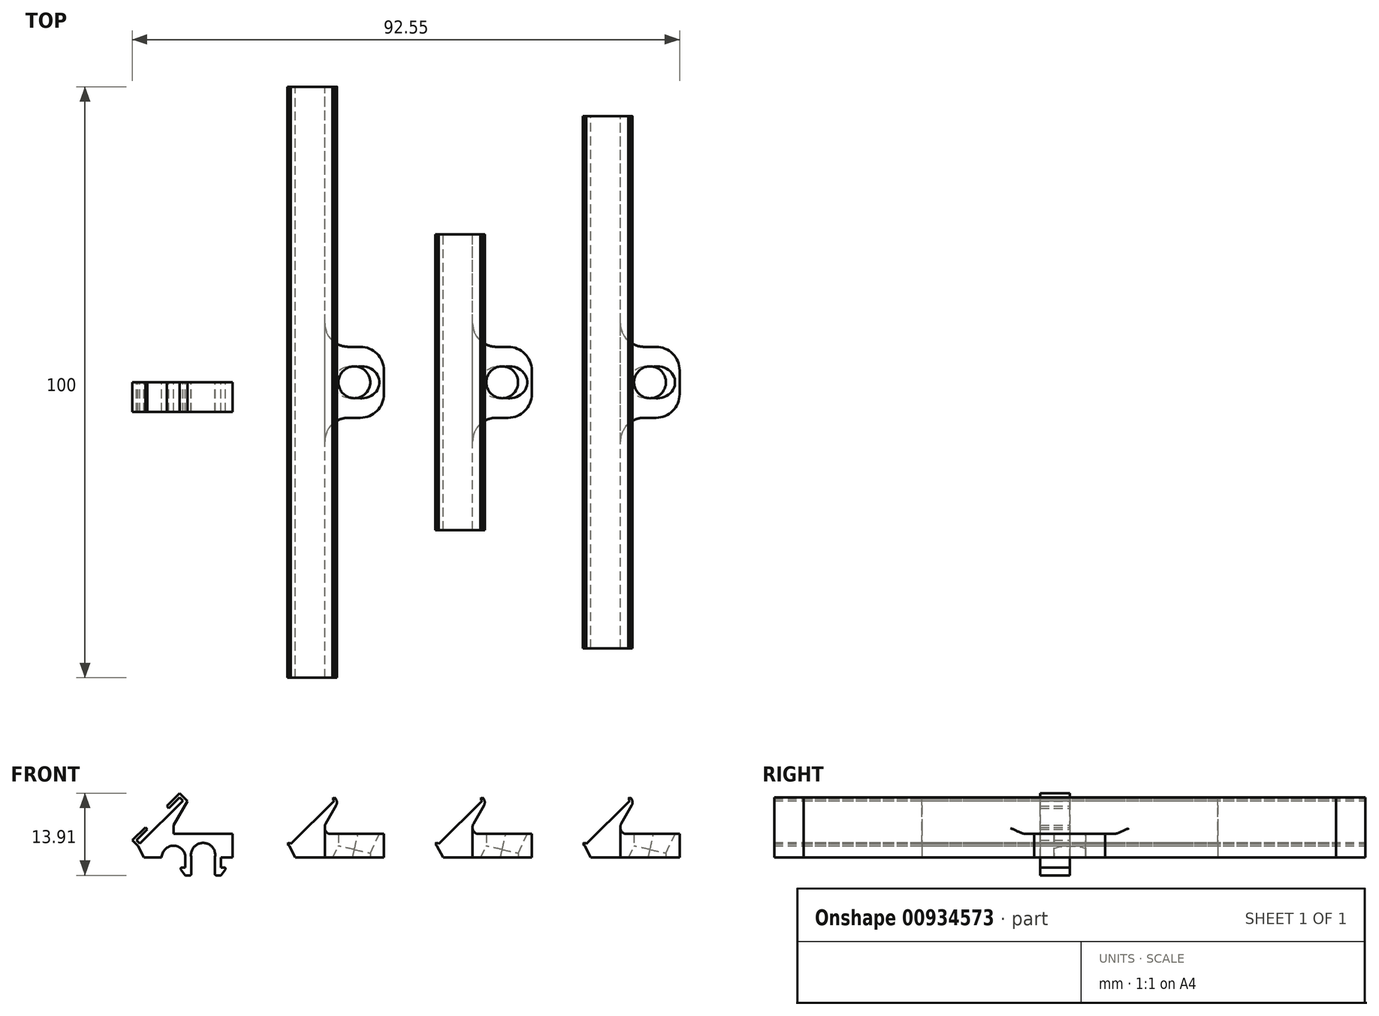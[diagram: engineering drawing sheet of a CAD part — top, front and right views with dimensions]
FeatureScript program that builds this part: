
annotation { "Feature Type Name" : "Feature", "Feature Type Description" : "" }
export const myFeature = defineFeature(function(context is Context, id is Id, definition is map)
    precondition{}
    {
        {
            var Q0;
            Q0=qCreatedBy(makeId("Front.planeOp"),FACE);
            var sketch = newSketch(context, id + "F0", { "sketchPlane" : qUnion([Q0])});
            skLineSegment(sketch, "E0", {"start": v(0, 0) * mm, "end": v(-10, 0) * mm});
            skLineSegment(sketch, "E1", {"start": v(-11.04, 2.57) * mm, "end": v(-10.76, 2.28) * mm});
            skLineSegment(sketch, "E2", {"start": v(-10.76, 2.28) * mm, "end": v(-3.4, 9.64) * mm});
            skLineSegment(sketch, "E3", {"start": v(-3.4, 9.64) * mm, "end": v(-3.69, 9.92) * mm});
            skLineSegment(sketch, "E4", {"start": v(-11.04, 2.57) * mm, "end": v(-11.33, 2.28) * mm});
            skLineSegment(sketch, "E5", {"start": v(-2.7, 4) * mm, "end": v(5, 4) * mm});
            skLineSegment(sketch, "E6", {"start": v(5, 4) * mm, "end": v(5, 0) * mm});
            skLineSegment(sketch, "E7", {"start": v(5, 0) * mm, "end": v(0, 0) * mm});
            skLineSegment(sketch, "E8", {"start": v(-2.7, 9.5) * mm, "end": v(-5, 5.5) * mm});
            skLineSegment(sketch, "E9", {"start": v(-5, 5.5) * mm, "end": v(-5, 4) * mm});
            skLineSegment(sketch, "E10", {"start": v(-5, 4) * mm, "end": v(-2.7, 4) * mm});
            skLineSegment(sketch, "E11", {"start": v(-3.69, 9.92) * mm, "end": v(-3.4, 10.2) * mm});
            skLineSegment(sketch, "E12", {"start": v(-3.4, 10.2) * mm, "end": v(-2.7, 9.5) * mm});
            skLineSegment(sketch, "E13", {"start": v(-2.7, 4) * mm, "end": v(-2.7, 0) * mm});
            skLineSegment(sketch, "E14", {"start": v(-5, 4) * mm, "end": v(-5, 0) * mm});
            skLineSegment(sketch, "E15", {"start": v(-11.33, 2.28) * mm, "end": v(-11.04, 2) * mm});
            skLineSegment(sketch, "E16", {"start": v(-11.04, 2) * mm, "end": v(-10, 0) * mm});
            skLineSegment(sketch, "E17", {"start": v(0, 0) * mm, "end": v(6.82, 14.44) * mm, "construction": true});
            skSolve(sketch);
        }
        {
            var Q0;
            Q0=makeQuery(id+"F0.imprint","IMPRINT",FACE,{"disambiguationData":[TD([[makeQuery(id+"F0.imprint","IMPRINT",EDGE,{"derivedFrom":sQuery(id+"F0.wireOp",EDGE,"E1")}),-1.0]])]});
            var Q1;
            Q1=makeQuery(id+"F0.imprint","IMPRINT",FACE,{"disambiguationData":[TD([[makeQuery(id+"F0.imprint","IMPRINT",EDGE,{"derivedFrom":sQuery(id+"F0.wireOp",EDGE,"E5")}),-1.0]])]});
            var Q2;
            Q2=makeQuery(id+"F0.imprint","IMPRINT",FACE,{"disambiguationData":[TD([[makeQuery(id+"F0.imprint","IMPRINT",EDGE,{"derivedFrom":sQuery(id+"F0.wireOp",EDGE,"E10")}),-1.0]])]});
            extrude(context, id + "F1", {"entities" : qUnion([Q0, Q1, Q2]), "endBound" : BoundingType.SYMMETRIC, "depth" : 12 * mm, "offsetDistance" : 25 * mm});
        }
        {
            var Q0;
            Q0=qCreatedBy(makeId("Top.planeOp"),FACE);
            var sketch = newSketch(context, id + "F2", { "sketchPlane" : qUnion([Q0])});
            skCircle(sketch, "E18", {"center": v(0, 0) * mm, "radius": 2.7 * mm});
            skSolve(sketch);
        }
        {
            var Q0;
            Q0=makeQuery(id+"F2.imprint","IMPRINT",FACE,{"disambiguationData":[TD([[makeQuery(id+"F2.imprint","IMPRINT",EDGE,{"derivedFrom":sQuery(id+"F2.wireOp",EDGE,"E18")}),1.0]])]});
            extrude(context, id + "F3", {"entities" : qUnion([Q0]), "operationType" : NewBodyOperationType.REMOVE, "depth" : 25 * mm, "offsetDistance" : 25 * mm});
        }
        {
            var Q0;
            Q0=makeQuery(id+"F0.imprint","IMPRINT",FACE,{"disambiguationData":[TD([[makeQuery(id+"F0.imprint","IMPRINT",EDGE,{"derivedFrom":sQuery(id+"F0.wireOp",EDGE,"E1")}),-1.0]])]});
            extrude(context, id + "F4", {"entities" : qUnion([Q0]), "operationType" : NewBodyOperationType.ADD, "endBound" : BoundingType.SYMMETRIC, "depth" : 100 * mm, "offsetDistance" : 25 * mm});
        }
        {
            var Q0;
            {var subQ0=sQuery(id+"F0.wireOp",EDGE,"E9");Q0=makeQuery(id+"F4.boolean.opBoolean","INTERSECT",EDGE,{"derivedFrom":[makeQuery(id+"F1.opExtrude","CAP_FACE",FACE,{"disambiguationData":[OSD([sQuery(id+"F0.wireOp",EDGE,"E0"),sQuery(id+"F0.wireOp",EDGE,"E1"),sQuery(id+"F0.wireOp",EDGE,"E2"),sQuery(id+"F0.wireOp",EDGE,"E3"),sQuery(id+"F0.wireOp",EDGE,"E4"),sQuery(id+"F0.wireOp",EDGE,"E5"),sQuery(id+"F0.wireOp",EDGE,"E6"),sQuery(id+"F0.wireOp",EDGE,"E7"),sQuery(id+"F0.wireOp",EDGE,"E8"),subQ0,sQuery(id+"F0.wireOp",EDGE,"E10"),sQuery(id+"F0.wireOp",EDGE,"E11"),sQuery(id+"F0.wireOp",EDGE,"E12"),sQuery(id+"F0.wireOp",EDGE,"E15"),sQuery(id+"F0.wireOp",EDGE,"E16")])],"isStart":true}),makeQuery(id+"F4.opExtrude","SWEPT_FACE",FACE,{"disambiguationData":[OSD([subQ0,sQuery(id+"F0.wireOp",EDGE,"E14")])]})]});}
            var Q1;
            Q1=makeQuery(id+"F1.opExtrude","CAP_EDGE",EDGE,{"disambiguationData":[OSD([sQuery(id+"F0.wireOp",EDGE,"E6")])],"isStart":true});
            var Q2;
            Q2=makeQuery(id+"F1.opExtrude","CAP_EDGE",EDGE,{"disambiguationData":[OSD([sQuery(id+"F0.wireOp",EDGE,"E6")])],"isStart":false});
            var Q3;
            {var subQ0=sQuery(id+"F0.wireOp",EDGE,"E9");Q3=makeQuery(id+"F4.boolean.opBoolean","INTERSECT",EDGE,{"derivedFrom":[makeQuery(id+"F1.opExtrude","CAP_FACE",FACE,{"disambiguationData":[OSD([sQuery(id+"F0.wireOp",EDGE,"E0"),sQuery(id+"F0.wireOp",EDGE,"E1"),sQuery(id+"F0.wireOp",EDGE,"E2"),sQuery(id+"F0.wireOp",EDGE,"E3"),sQuery(id+"F0.wireOp",EDGE,"E4"),sQuery(id+"F0.wireOp",EDGE,"E5"),sQuery(id+"F0.wireOp",EDGE,"E6"),sQuery(id+"F0.wireOp",EDGE,"E7"),sQuery(id+"F0.wireOp",EDGE,"E8"),subQ0,sQuery(id+"F0.wireOp",EDGE,"E10"),sQuery(id+"F0.wireOp",EDGE,"E11"),sQuery(id+"F0.wireOp",EDGE,"E12"),sQuery(id+"F0.wireOp",EDGE,"E15"),sQuery(id+"F0.wireOp",EDGE,"E16")])],"isStart":false}),makeQuery(id+"F4.opExtrude","SWEPT_FACE",FACE,{"disambiguationData":[OSD([subQ0,sQuery(id+"F0.wireOp",EDGE,"E14")])]})]});}
            fillet(context, id + "F5", {"entities" : qUnion([Q0, Q1, Q2, Q3]), "radius" : 4 * mm, "tangentPropagation" : true, "allowEdgeOverflow" : false});
        }
        {
            var Q0;
            {var subQ0=sQuery(id+"F0.wireOp",EDGE,"E12");var subQ1=sQuery(id+"F0.wireOp",EDGE,"E8");var subQ2=sQuery(id+"F0.wireOp",EDGE,"E16");var subQ3=sQuery(id+"F0.wireOp",EDGE,"E15");var subQ4=sQuery(id+"F0.wireOp",EDGE,"E11");var subQ5=sQuery(id+"F0.wireOp",EDGE,"E10");var subQ6=sQuery(id+"F0.wireOp",EDGE,"E9");var subQ7=sQuery(id+"F0.wireOp",EDGE,"E7");var subQ8=sQuery(id+"F0.wireOp",EDGE,"E6");var subQ9=sQuery(id+"F0.wireOp",EDGE,"E5");var subQ10=sQuery(id+"F0.wireOp",EDGE,"E4");var subQ11=sQuery(id+"F0.wireOp",EDGE,"E3");var subQ12=sQuery(id+"F0.wireOp",EDGE,"E2");var subQ13=sQuery(id+"F0.wireOp",EDGE,"E1");var subQ14=sQuery(id+"F0.wireOp",EDGE,"E0");var subQ17=makeQuery(id+"F1.opExtrude","SWEPT_EDGE",EDGE,{"disambiguationData":[OSD([subQ1,subQ0])]});Q0=makeQuery(id+"F4.boolean.opBoolean","MERGE",EDGE,{"derivedFrom":[makeQuery(id+"F3.boolean.opBoolean","SPLIT",EDGE,{"disambiguationData":[TD([makeQuery(id+"F1.opExtrude","CAP_FACE",FACE,{"disambiguationData":[OSD([subQ14,subQ13,subQ12,subQ11,subQ10,subQ9,subQ8,subQ7,subQ1,subQ6,subQ5,subQ4,subQ0,subQ3,subQ2])],"isStart":true})])],"derivedFrom":subQ17}),makeQuery(id+"F3.boolean.opBoolean","SPLIT",EDGE,{"disambiguationData":[TD([makeQuery(id+"F1.opExtrude","CAP_FACE",FACE,{"disambiguationData":[OSD([subQ14,subQ13,subQ12,subQ11,subQ10,subQ9,subQ8,subQ7,subQ1,subQ6,subQ5,subQ4,subQ0,subQ3,subQ2])],"isStart":false})])],"derivedFrom":subQ17}),makeQuery(id+"F4.opExtrude","SWEPT_EDGE",EDGE,{"disambiguationData":[OSD([subQ1,subQ0])]})]});}
            var Q1;
            {var subQ0=sQuery(id+"F0.wireOp",EDGE,"E9");var subQ1=sQuery(id+"F0.wireOp",EDGE,"E8");Q1=makeQuery(id+"F4.boolean.opBoolean","MERGE",EDGE,{"derivedFrom":[makeQuery(id+"F1.opExtrude","SWEPT_EDGE",EDGE,{"disambiguationData":[OSD([subQ1,subQ0])]}),makeQuery(id+"F4.opExtrude","SWEPT_EDGE",EDGE,{"disambiguationData":[OSD([subQ1,subQ0])]})]});}
            var Q2;
            Q2=makeQuery(id+"F1.opExtrude","SWEPT_EDGE",EDGE,{"disambiguationData":[OSD([sQuery(id+"F0.wireOp",EDGE,"E9"),sQuery(id+"F0.wireOp",EDGE,"E10"),sQuery(id+"F0.wireOp",EDGE,"E14")])]});
            fillet(context, id + "F6", {"entities" : qUnion([Q0, Q1, Q2]), "radius" : 1 * mm, "tangentPropagation" : true, "allowEdgeOverflow" : false});
        }
        {
            var Q0;
            Q0=sQuery(id+"F0.wireOp",EDGE,"E17");
            cPlane(context, id + "F7", {"entities" : qUnion([Q0]), "cplaneType" : CPlaneType.MID_PLANE, "offset" : 25 * mm, "width" : 150 * mm, "height" : 150 * mm});
        }
        {
            var Q0;
            Q0=qCreatedBy(id+"F7.planeOp",FACE);
            var sketch = newSketch(context, id + "F8", { "sketchPlane" : qUnion([Q0])});
            skCircle(sketch, "E19", {"center": v(-0.58, 0) * mm, "radius": 2.7 * mm});
            skSolve(sketch);
        }
        {
            var Q0;
            Q0=makeQuery(id+"F8.imprint","IMPRINT",FACE,{"disambiguationData":[TD([[makeQuery(id+"F8.imprint","IMPRINT",EDGE,{"derivedFrom":sQuery(id+"F8.wireOp",EDGE,"E19")}),1.0]])]});
            extrude(context, id + "F9", {"entities" : qUnion([Q0]), "operationType" : NewBodyOperationType.REMOVE, "oppositeDirection" : true, "depth" : 25 * mm, "offsetDistance" : 25 * mm});
        }
        {
            var Q0;
            Q0=makeQuery(id+"F1.opExtrude","SWEPT_BODY",BODY,{"disambiguationData":[OSD([sQuery(id+"F0.wireOp",EDGE,"E0"),sQuery(id+"F0.wireOp",EDGE,"E1"),sQuery(id+"F0.wireOp",EDGE,"E2"),sQuery(id+"F0.wireOp",EDGE,"E3"),sQuery(id+"F0.wireOp",EDGE,"E4"),sQuery(id+"F0.wireOp",EDGE,"E5"),sQuery(id+"F0.wireOp",EDGE,"E6"),sQuery(id+"F0.wireOp",EDGE,"E7"),sQuery(id+"F0.wireOp",EDGE,"E8"),sQuery(id+"F0.wireOp",EDGE,"E9"),sQuery(id+"F0.wireOp",EDGE,"E10"),sQuery(id+"F0.wireOp",EDGE,"E11"),sQuery(id+"F0.wireOp",EDGE,"E12"),sQuery(id+"F0.wireOp",EDGE,"E15"),sQuery(id+"F0.wireOp",EDGE,"E16")])]});
            transform(context, id + "F10", {"entities" : qUnion([Q0]), "transformType" : TransformType.TRANSLATION_3D, "dx" : 25 * mm, "dy" : 0 * mm, "dz" : 0 * mm, "makeCopy" : true});
        }
        {
            var Q0;
            Q0=makeQuery(id+"F10.opPattern","COPY",FACE,{"derivedFrom":makeQuery(id+"F4.opExtrude","CAP_FACE",FACE,{"disambiguationData":[OSD([sQuery(id+"F0.wireOp",EDGE,"E0"),sQuery(id+"F0.wireOp",EDGE,"E1"),sQuery(id+"F0.wireOp",EDGE,"E2"),sQuery(id+"F0.wireOp",EDGE,"E3"),sQuery(id+"F0.wireOp",EDGE,"E4"),sQuery(id+"F0.wireOp",EDGE,"E8"),sQuery(id+"F0.wireOp",EDGE,"E9"),sQuery(id+"F0.wireOp",EDGE,"E11"),sQuery(id+"F0.wireOp",EDGE,"E12"),sQuery(id+"F0.wireOp",EDGE,"E14"),sQuery(id+"F0.wireOp",EDGE,"E15"),sQuery(id+"F0.wireOp",EDGE,"E16")])],"isStart":false}),"instanceName":"1"});
            var Q1;
            Q1=makeQuery(id+"F10.opPattern","COPY",FACE,{"derivedFrom":makeQuery(id+"F4.opExtrude","CAP_FACE",FACE,{"disambiguationData":[OSD([sQuery(id+"F0.wireOp",EDGE,"E0"),sQuery(id+"F0.wireOp",EDGE,"E1"),sQuery(id+"F0.wireOp",EDGE,"E2"),sQuery(id+"F0.wireOp",EDGE,"E3"),sQuery(id+"F0.wireOp",EDGE,"E4"),sQuery(id+"F0.wireOp",EDGE,"E8"),sQuery(id+"F0.wireOp",EDGE,"E9"),sQuery(id+"F0.wireOp",EDGE,"E11"),sQuery(id+"F0.wireOp",EDGE,"E12"),sQuery(id+"F0.wireOp",EDGE,"E14"),sQuery(id+"F0.wireOp",EDGE,"E15"),sQuery(id+"F0.wireOp",EDGE,"E16")])],"isStart":true}),"instanceName":"1"});
            extrude(context, id + "F11", {"entities" : qUnion([Q0, Q1]), "operationType" : NewBodyOperationType.REMOVE, "endBound" : BoundingType.SYMMETRIC, "oppositeDirection" : true, "depth" : 50 * mm, "offsetDistance" : 25 * mm});
        }
        {
            var Q0;
            Q0=qCreatedBy(makeId("Front.planeOp"),FACE);
            var sketch = newSketch(context, id + "F12", { "sketchPlane" : qUnion([Q0])});
            skLineSegment(sketch, "E20", {"start": v(-25.58, 0) * mm, "end": v(-35.58, 0) * mm});
            skLineSegment(sketch, "E21", {"start": v(-36.84, 2.92) * mm, "end": v(-36.27, 2.35) * mm});
            skLineSegment(sketch, "E22", {"start": v(-36.27, 2.35) * mm, "end": v(-28.99, 9.64) * mm});
            skLineSegment(sketch, "E23", {"start": v(-28.99, 9.64) * mm, "end": v(-29.56, 10.2) * mm});
            skLineSegment(sketch, "E24", {"start": v(-36.84, 2.92) * mm, "end": v(-37.2, 2.57) * mm});
            skLineSegment(sketch, "E25", {"start": v(-28.28, 4) * mm, "end": v(-20.58, 4) * mm});
            skLineSegment(sketch, "E26", {"start": v(-20.58, 4) * mm, "end": v(-20.58, 0) * mm});
            skLineSegment(sketch, "E27", {"start": v(-20.58, 0) * mm, "end": v(-25.58, 0) * mm});
            skLineSegment(sketch, "E28", {"start": v(-28.21, 9.57) * mm, "end": v(-30.58, 5.5) * mm});
            skLineSegment(sketch, "E29", {"start": v(-30.58, 5.5) * mm, "end": v(-30.58, 4) * mm});
            skLineSegment(sketch, "E30", {"start": v(-30.58, 4) * mm, "end": v(-28.28, 4) * mm});
            skLineSegment(sketch, "E31", {"start": v(-29.56, 10.2) * mm, "end": v(-29.2, 10.56) * mm});
            skLineSegment(sketch, "E32", {"start": v(-29.2, 10.56) * mm, "end": v(-28.21, 9.57) * mm});
            skLineSegment(sketch, "E33", {"start": v(-28.28, 4) * mm, "end": v(-28.28, 0) * mm});
            skLineSegment(sketch, "E34", {"start": v(-30.58, 4) * mm, "end": v(-30.58, 0) * mm});
            skLineSegment(sketch, "E35", {"start": v(-37.2, 2.57) * mm, "end": v(-36.63, 2) * mm});
            skLineSegment(sketch, "E36", {"start": v(-36.63, 2) * mm, "end": v(-35.58, 0) * mm});
            skLineSegment(sketch, "E37", {"start": v(-25.58, 0) * mm, "end": v(-25.58, 24.72) * mm, "construction": true});
            skLineSegment(sketch, "E38", {"start": v(-25.58, 15.93) * mm, "end": v(-25.58, -11.5) * mm, "construction": true});
            skLineSegment(sketch, "E39", {"start": v(-27.58, 0) * mm, "end": v(-27.58, -3) * mm});
            skLineSegment(sketch, "E40", {"start": v(-27.58, -3) * mm, "end": v(-28.58, -3) * mm});
            skLineSegment(sketch, "E41", {"start": v(-28.58, -3) * mm, "end": v(-29.58, -1.7) * mm});
            skLineSegment(sketch, "E42", {"start": v(-29.58, -1.7) * mm, "end": v(-28.58, -1.7) * mm});
            skLineSegment(sketch, "E43", {"start": v(-28.58, -1.7) * mm, "end": v(-28.58, 0) * mm});
            skArc(sketch, "E44", {"start": v(-27.58, 0) * mm, "mid": v(-25.58, 2.49) * mm, "end": v(-23.58, 0) * mm});
            skArc(sketch, "E45", {"start": v(-28.58, 0) * mm, "mid": v(-30.58, 2) * mm, "end": v(-32.58, 0) * mm});
            skLineSegment(sketch, "E46", {"start": v(-36.84, 2.92) * mm, "end": v(-35, 4.76) * mm});
            skLineSegment(sketch, "E47", {"start": v(-35, 4.76) * mm, "end": v(-35.35, 5.11) * mm});
            skLineSegment(sketch, "E48", {"start": v(-35.35, 5.11) * mm, "end": v(-37.55, 2.92) * mm});
            skLineSegment(sketch, "E49", {"start": v(-37.55, 2.92) * mm, "end": v(-37.2, 2.57) * mm});
            skLineSegment(sketch, "E50", {"start": v(-29.56, 10.2) * mm, "end": v(-31.4, 8.36) * mm});
            skLineSegment(sketch, "E51", {"start": v(-31.4, 8.36) * mm, "end": v(-31.75, 8.72) * mm});
            skLineSegment(sketch, "E52", {"start": v(-31.75, 8.72) * mm, "end": v(-29.56, 10.9) * mm});
            skLineSegment(sketch, "E53", {"start": v(-29.56, 10.9) * mm, "end": v(-29.2, 10.56) * mm});
            skLineSegment(sketch, "E54.MirrorCS", {"start": v(-23.58, 0) * mm, "end": v(-23.58, -3) * mm});
            skLineSegment(sketch, "E55.MirrorCS", {"start": v(-23.58, -3) * mm, "end": v(-22.58, -3) * mm});
            skLineSegment(sketch, "E56.MirrorCS", {"start": v(-22.58, -3) * mm, "end": v(-21.58, -1.7) * mm});
            skLineSegment(sketch, "E57.MirrorCS", {"start": v(-21.58, -1.7) * mm, "end": v(-22.58, -1.7) * mm});
            skLineSegment(sketch, "E58.MirrorCS", {"start": v(-22.58, -1.7) * mm, "end": v(-22.58, 0) * mm});
            skSolve(sketch);
        }
        {
            var Q0;
            Q0=makeQuery(id+"F12.imprint","IMPRINT",FACE,{"disambiguationData":[TD([[makeQuery(id+"F12.imprint","IMPRINT",EDGE,{"derivedFrom":sQuery(id+"F12.wireOp",EDGE,"E21")}),-1.0]])]});
            var Q1;
            Q1=makeQuery(id+"F12.imprint","IMPRINT",FACE,{"disambiguationData":[TD([[makeQuery(id+"F12.imprint","IMPRINT",EDGE,{"derivedFrom":sQuery(id+"F12.wireOp",EDGE,"E24")}),-1.0]])]});
            var Q2;
            Q2=makeQuery(id+"F12.imprint","IMPRINT",FACE,{"disambiguationData":[TD([[makeQuery(id+"F12.imprint","IMPRINT",EDGE,{"derivedFrom":sQuery(id+"F12.wireOp",EDGE,"E31")}),1.0]])]});
            var Q3;
            {var subQ1=sQuery(id+"F12.wireOp",EDGE,"E30");Q3=makeQuery(id+"F12.imprint","IMPRINT",FACE,{"disambiguationData":[TD([[makeQuery(id+"F12.imprint","IMPRINT",EDGE,{"derivedFrom":subQ1}),-1.0]])]});}
            var Q4;
            Q4=makeQuery(id+"F12.imprint","IMPRINT",FACE,{"disambiguationData":[TD([[makeQuery(id+"F12.imprint","IMPRINT",EDGE,{"derivedFrom":sQuery(id+"F12.wireOp",EDGE,"E25")}),-1.0]])]});
            var Q5;
            {var subQ0=sQuery(id+"F12.wireOp",EDGE,"E54.MirrorCS");Q5=makeQuery(id+"F12.imprint","IMPRINT",FACE,{"disambiguationData":[TD([[makeQuery(id+"F12.imprint","IMPRINT",EDGE,{"derivedFrom":subQ0}),1.0]])]});}
            var Q6;
            {var subQ0=sQuery(id+"F12.wireOp",EDGE,"E39");Q6=makeQuery(id+"F12.imprint","IMPRINT",FACE,{"disambiguationData":[TD([[makeQuery(id+"F12.imprint","IMPRINT",EDGE,{"derivedFrom":subQ0}),-1.0]])]});}
            extrude(context, id + "F13", {"entities" : qUnion([Q0, Q1, Q2, Q3, Q4, Q5, Q6]), "depth" : 5 * mm, "offsetDistance" : 25 * mm});
        }
        {
            var Q0;
            Q0=makeQuery(id+"F13.opExtrude","SWEPT_EDGE",EDGE,{"disambiguationData":[OSD([sQuery(id+"F12.wireOp",EDGE,"E56.MirrorCS"),sQuery(id+"F12.wireOp",EDGE,"E57.MirrorCS")])]});
            var Q1;
            Q1=makeQuery(id+"F13.opExtrude","SWEPT_EDGE",EDGE,{"disambiguationData":[OSD([sQuery(id+"F12.wireOp",EDGE,"E41"),sQuery(id+"F12.wireOp",EDGE,"E42")])]});
            var Q2;
            Q2=makeQuery(id+"F13.opExtrude","SWEPT_EDGE",EDGE,{"disambiguationData":[OSD([sQuery(id+"F12.wireOp",EDGE,"E54.MirrorCS"),sQuery(id+"F12.wireOp",EDGE,"E55.MirrorCS")])]});
            var Q3;
            Q3=makeQuery(id+"F13.opExtrude","SWEPT_EDGE",EDGE,{"disambiguationData":[OSD([sQuery(id+"F12.wireOp",EDGE,"E39"),sQuery(id+"F12.wireOp",EDGE,"E40")])]});
            fillet(context, id + "F14", {"entities" : qUnion([Q0, Q1, Q2, Q3]), "radius" : 0.2 * mm, "tangentPropagation" : true, "allowEdgeOverflow" : false});
        }
        {
            var Q0;
            Q0=makeQuery(id+"F10.opPattern","COPY",BODY,{"derivedFrom":makeQuery(id+"F1.opExtrude","SWEPT_BODY",BODY,{"disambiguationData":[OSD([sQuery(id+"F0.wireOp",EDGE,"E0"),sQuery(id+"F0.wireOp",EDGE,"E1"),sQuery(id+"F0.wireOp",EDGE,"E2"),sQuery(id+"F0.wireOp",EDGE,"E3"),sQuery(id+"F0.wireOp",EDGE,"E4"),sQuery(id+"F0.wireOp",EDGE,"E5"),sQuery(id+"F0.wireOp",EDGE,"E6"),sQuery(id+"F0.wireOp",EDGE,"E7"),sQuery(id+"F0.wireOp",EDGE,"E8"),sQuery(id+"F0.wireOp",EDGE,"E9"),sQuery(id+"F0.wireOp",EDGE,"E10"),sQuery(id+"F0.wireOp",EDGE,"E11"),sQuery(id+"F0.wireOp",EDGE,"E12"),sQuery(id+"F0.wireOp",EDGE,"E15"),sQuery(id+"F0.wireOp",EDGE,"E16")])]}),"instanceName":"1"});
            transform(context, id + "F15", {"entities" : qUnion([Q0]), "transformType" : TransformType.TRANSLATION_3D, "dx" : 25 * mm, "dy" : 0 * mm, "dz" : 0 * mm, "makeCopy" : true});
        }
        {
            var Q0;
            {var subQ0=sQuery(id+"F0.wireOp",EDGE,"E16");var subQ1=sQuery(id+"F0.wireOp",EDGE,"E15");var subQ2=sQuery(id+"F0.wireOp",EDGE,"E14");var subQ3=sQuery(id+"F0.wireOp",EDGE,"E12");var subQ4=sQuery(id+"F0.wireOp",EDGE,"E11");var subQ5=sQuery(id+"F0.wireOp",EDGE,"E9");var subQ6=sQuery(id+"F0.wireOp",EDGE,"E8");var subQ7=sQuery(id+"F0.wireOp",EDGE,"E4");var subQ8=sQuery(id+"F0.wireOp",EDGE,"E3");var subQ9=sQuery(id+"F0.wireOp",EDGE,"E2");var subQ10=sQuery(id+"F0.wireOp",EDGE,"E1");var subQ11=sQuery(id+"F0.wireOp",EDGE,"E0");Q0=makeQuery(id+"F15.opPattern","COPY",FACE,{"derivedFrom":makeQuery(id+"F11.boolean.opBoolean","COPY",FACE,{"derivedFrom":makeQuery(id+"F11.opExtrude","CAP_FACE",FACE,{"disambiguationData":[OSD([subQ11,subQ10,subQ9,subQ8,subQ7,subQ6,subQ5,subQ4,subQ3,subQ2,subQ1,subQ0]),TDD([makeQuery(id+"F10.opPattern","COPY",FACE,{"derivedFrom":makeQuery(id+"F4.opExtrude","CAP_FACE",FACE,{"disambiguationData":[OSD([subQ11,subQ10,subQ9,subQ8,subQ7,subQ6,subQ5,subQ4,subQ3,subQ2,subQ1,subQ0])],"isStart":false}),"instanceName":"1"})])],"isStart":false})}),"instanceName":"1"});}
            var Q1;
            {var subQ0=sQuery(id+"F0.wireOp",EDGE,"E16");var subQ1=sQuery(id+"F0.wireOp",EDGE,"E15");var subQ2=sQuery(id+"F0.wireOp",EDGE,"E14");var subQ3=sQuery(id+"F0.wireOp",EDGE,"E12");var subQ4=sQuery(id+"F0.wireOp",EDGE,"E11");var subQ5=sQuery(id+"F0.wireOp",EDGE,"E9");var subQ6=sQuery(id+"F0.wireOp",EDGE,"E8");var subQ7=sQuery(id+"F0.wireOp",EDGE,"E4");var subQ8=sQuery(id+"F0.wireOp",EDGE,"E3");var subQ9=sQuery(id+"F0.wireOp",EDGE,"E2");var subQ10=sQuery(id+"F0.wireOp",EDGE,"E1");var subQ11=sQuery(id+"F0.wireOp",EDGE,"E0");Q1=makeQuery(id+"F15.opPattern","COPY",FACE,{"derivedFrom":makeQuery(id+"F11.boolean.opBoolean","COPY",FACE,{"derivedFrom":makeQuery(id+"F11.opExtrude","CAP_FACE",FACE,{"disambiguationData":[OSD([subQ11,subQ10,subQ9,subQ8,subQ7,subQ6,subQ5,subQ4,subQ3,subQ2,subQ1,subQ0]),TDD([makeQuery(id+"F10.opPattern","COPY",FACE,{"derivedFrom":makeQuery(id+"F4.opExtrude","CAP_FACE",FACE,{"disambiguationData":[OSD([subQ11,subQ10,subQ9,subQ8,subQ7,subQ6,subQ5,subQ4,subQ3,subQ2,subQ1,subQ0])],"isStart":true}),"instanceName":"1"})])],"isStart":true})}),"instanceName":"1"});}
            extrude(context, id + "F16", {"entities" : qUnion([Q0, Q1]), "operationType" : NewBodyOperationType.ADD, "endBound" : BoundingType.SYMMETRIC, "depth" : 40 * mm, "offsetDistance" : 25 * mm});
        }
    });
